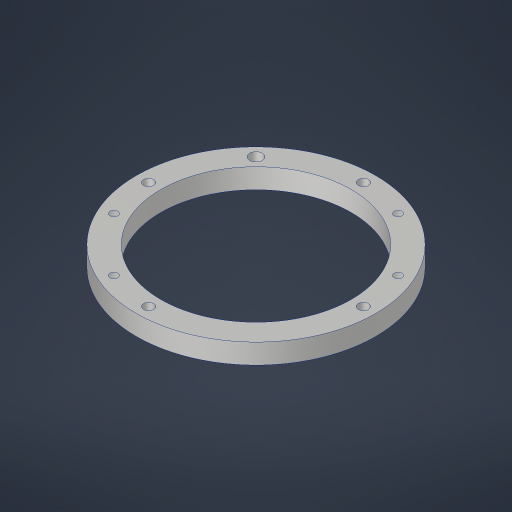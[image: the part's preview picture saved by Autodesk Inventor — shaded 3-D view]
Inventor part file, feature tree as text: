
AUTODESK INVENTOR PART (.ipt)
format: ipt  version: 2023.4 (Build 274418000, 418)  size: 241,664 bytes
history: native  units: in
note: dims shown in document units (in); Inventor stores cm internally (conversion verified against a paired STEP export)
features: sketch x4, hole x3, projected_geometry x2, extrude x1, pattern_circular x1
ambient origin geometry x8: Origin, YZ Plane, XZ Plane, XY Plane, X Axis, Y Axis, Z Axis, Center Point
bodies: Solid1 (feature_tree)
feature tree (11):
  extrude  "Extrusion1"  Depth=4.7244in
  hole  "Hole2"  [1 undecoded]
  pattern_circular  "Circular Pattern2"  Angle=45.0deg  [1 undecoded]
  hole  "Hole3"  [1 undecoded]
  hole  "Hole4"  [1 undecoded]
  sketch  "Sketch1"  dims[d0=2.7559in d1=4.7244in]
  sketch  "Sketch3"  dims[d2=0.3937in d3=0.0in]
  sketch  "Sketch4"  dims[d15=0.201in d16=0.75in d17=0.385in d18=0.25in d19=0.5635in d20=1.0in d21=0.8108in d22=1.5748in d23=360.0deg]
  sketch  "Sketch5"  dims[d25=1.5in d26=45.0deg d27=0.156in d28=0.38in d29=0.563in d30=0.12in d31=0.5635in d32=1.0in d33=0.8108in d34=45.0deg d35=0.249in d36=0.75in d37=0.563in d38=0.12in d39=0.5635in d40=1.0in d41=0.8108in d42=0.4803in d43=4.7244in d44=2.122in]
  projected_geometry  "Project Cut Edges2"
  projected_geometry  "Project Cut Edges3"
note: 4 required parameter values undecoded (feature->parameter linkage not recoverable at this tier; creation-order binding heuristic only, values carry confidence <= 0.55)
